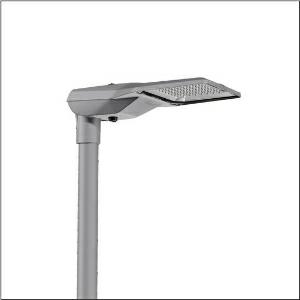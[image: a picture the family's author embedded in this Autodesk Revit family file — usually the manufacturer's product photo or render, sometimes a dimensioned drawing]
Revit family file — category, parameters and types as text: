
# Revit family: streetlight_sl_21_iq_midi___st1_5a_5xe3p31y08mb_5967
name_source: partatom
category: Lighting Fixtures
units: mm (PartAtom-declared; Revit-internal decimal feet)

## family parameters
Cut with Voids When Loaded = No
Host = Face
Light Source = No
Part Type = Normal
Room Calculation Point = No
Round Connector Dimension = Use Diameter
Shared = No

## types (1)
- --- (1 x LED, 18020 lm, 129.3 W, 3000K)
    Apparent Load = 129 VA
    CIE Flux Codes = 22 53 95 100 100
    Color Rendering = 70
    Color Temperature = 3000K
    Default Elevation = 1800 mm
    Description = Streetlight SL 21 iQ midi, mast luminaire, primary light control with lens, of PMMA, primary optical cover: cover, of toughened safety glass, transparent, light distribution: ST1.5a, light emission: direct distribution, primary light characteristic: asymmetric, installation type: post-top, side-entry, LED, High Power LED, rated luminous flux: 18.020lm, luminous efficacy: 139lm/W, light colour: 730, colour temperature: 3000K, control gear: iQ-Street Remote, D4i with power reduction, control: pre-setting: logarithmic dimming characteristic, Street-Remote, Auto-Match, Temp-Guard, Lumen-Switch, Night-Set, Smart-Wire, Light-Fading, Desk-Remote (wireless, voltage-free reading and setting of iQ features in the workshop via application-optimized NFC function/RFID function), optimised constant luminous flux control (CLO 2.0), mains connection: 230..240V, AC, 50/60Hz, start of lifetime: 129W, end of service life: 142W, reduction: 56W, luminaire housing, of diecast aluminium, powder-coated, Siteco® metallic grey (DB 702S), corrosivity category C5 mid according to DIN EN ISO 12944, please order mast flange separately, inclination adjustable: 0°, 5°, 10°, 15°, sealing non-destructively replaceable, multi-level sealing system, length: 644mm, width: 335mm, height: 110mm, mast flange for spigot size: 42mm (side-entry): 5XC10008XM4, 60/48mm (side-entry/post-top): 5XC10108XM2, 76/60mm (side-entry/post-top): 5XC10108XM1, mounting height: 4..8m, Smart Interface below and above, protection rating (complete): IP66, insulation class (complete): insulation class II (safety insulation), certification: CE, ENEC, ENEC+, VDE, impact resistance: IK10, permissible operating ambient temperature for outdoor applications: -40..+50°C, standard-compliant lighting for roads and squares, packaging unit: 1 piece

Light Distribution: ST1.5a
    Height = 111 mm
    Lamp = 1 x LED
    Lamp Light Flux = 18020 lm
    Lamp Power = 129.3 W
    Lamp count = 1
    Length = 644 mm
    Luminous efficacy = 139 lm/W
    Manufacturer = Siteco
    ModVariant = No
    Model = 5XE3P31Y08MB
    Number of Poles = 1
    OnlyDefault = Yes
    Power Factor = 1
    Product Name = Streetlight SL 21 iQ midi | ST1.5a
    Product group = mast luminaire | pylon top
    ProductGroupID = 6100
    Protection Class = Protection class II
    Protection Degree = IP 66
    RLX_Detail_Level = 1
    RLX_Emergency_Light_Flux = 0 lm
    RLX_Emergency_Type = 0
    RLX_Emergency_Type_DB = No
    RlxData = <blob elided: 94221 chars, md5=cab924b2>
    Socket = socket
    Standby Power = 0 W
    System Light Flux = 18021 lm
    System Power = 129 W
    Type Comments = factory setting: luminous flux: 100 % | dim-lin: 254 | 672 mA
    Type Image = l_1004304.jpg
    URL = http://relux.com
    VarID = @adj_133343
    Voltage = 0 V
    Weight = 0.00 kg
    Width = 336 mm

## geometry (parser evidence)
native form markers: Blend x4, Sweep x10
no freeform markers — native parametric forms only
